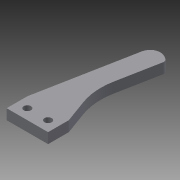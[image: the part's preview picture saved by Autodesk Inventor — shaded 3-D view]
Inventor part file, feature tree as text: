
AUTODESK INVENTOR PART (.ipt)
format: ipt  version: 2015 (Build 190159000, 159)  size: 97,792 bytes
history: native  units: mm
features: extrude x1, sketch x1
ambient origin geometry x8: Origin, YZ Plane, XZ Plane, XY Plane, X Axis, Y Axis, Z Axis, Center Point
bodies: Solid1 (feature_tree)
feature tree (2):
  extrude  "Extrusion1"  Depth=10.0mm
  sketch  "Sketch1"  dims[d0=5.0mm d1=10.0mm d2=3.5mm d3=3.5mm d4=5.0mm d5=10.0mm d6=10.0mm d7=10.0mm d8=10.0mm d9=20.0mm d10=19.198622mm d11=30.0mm d12=10.0mm d13=19.198622mm d14=30.0mm d15=2.0mm d16=5.0mm d17=5.0mm d18=0.0mm]
